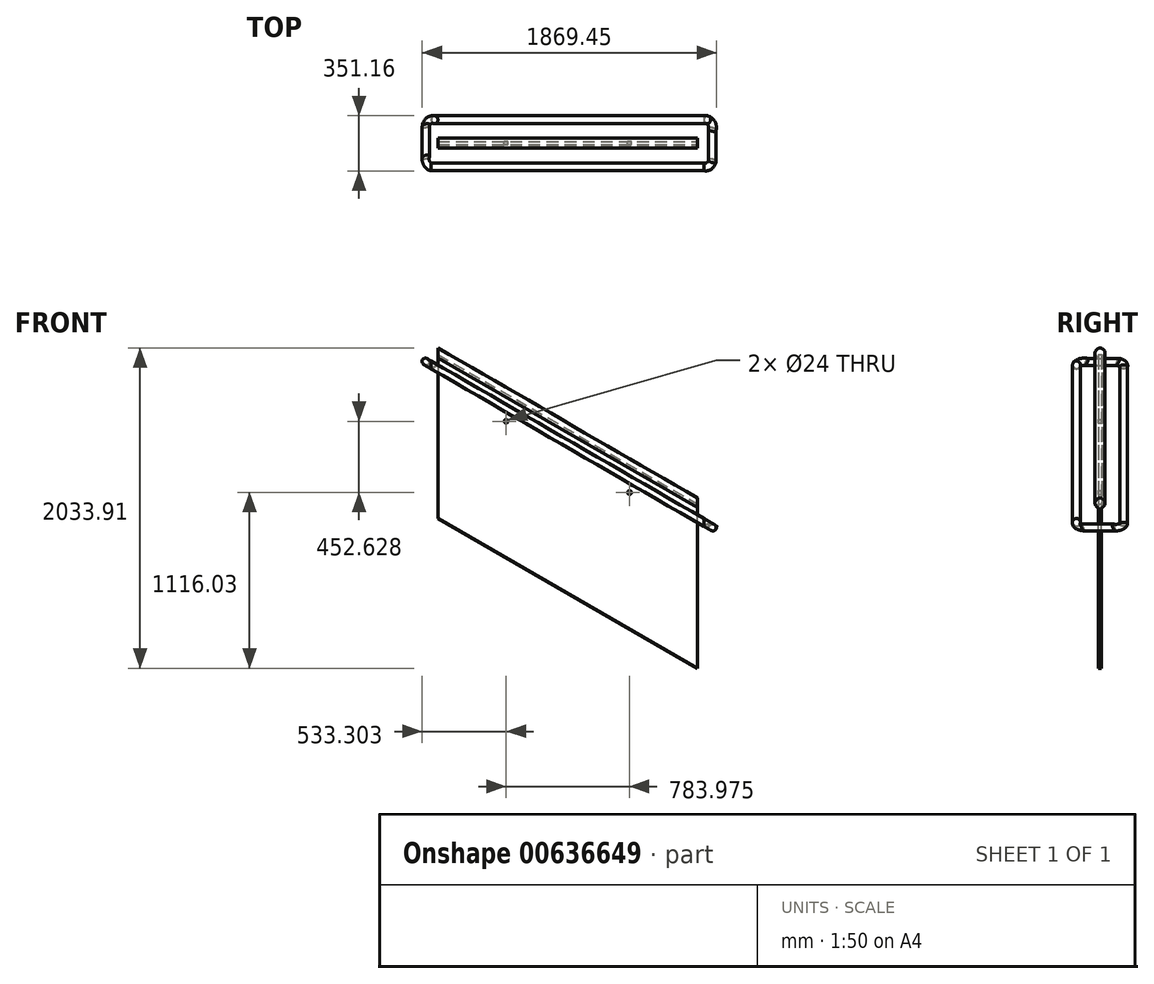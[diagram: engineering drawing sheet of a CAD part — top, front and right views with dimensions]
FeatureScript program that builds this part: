
annotation { "Feature Type Name" : "Feature", "Feature Type Description" : "" }
export const myFeature = defineFeature(function(context is Context, id is Id, definition is map)
    precondition{}
    {
        {
            var Q0;
            Q0=qCreatedBy(makeId("Front.planeOp"),FACE);
            var sketch = newSketch(context, id + "F0", { "sketchPlane" : qUnion([Q0])});
            skLineSegment(sketch, "E0", {"start": v(0, 0) * mm, "end": v(1650, -952.63) * mm});
            skLineSegment(sketch, "E1", {"start": v(1650, -952.63) * mm, "end": v(1650, 86.6) * mm});
            skLineSegment(sketch, "E2", {"start": v(1650, 86.6) * mm, "end": v(0, 1039.23) * mm});
            skLineSegment(sketch, "E3.0", {"start": v(1650, -86.6) * mm, "end": v(0, 866.03) * mm, "construction": true});
            skCircle(sketch, "E4", {"center": v(433.01, 616.03) * mm, "radius": 12 * mm});
            skCircle(sketch, "E5", {"center": v(1216.99, 163.4) * mm, "radius": 12 * mm});
            skLineSegment(sketch, "E6", {"start": v(0, 1039.23) * mm, "end": v(0, 0) * mm});
            skSolve(sketch);
        }
        {
            var Q0;
            Q0=qSketchRegion(id+"F0",true);
            extrude(context, id + "F1", {"entities" : qUnion([Q0]), "endBound" : BoundingType.SYMMETRIC, "depth" : 19 * mm, "offsetDistance" : 25 * mm});
        }
        {
            var Q0;
            Q0=qCreatedBy(makeId("Front.planeOp"),FACE);
            var sketch = newSketch(context, id + "F2", { "sketchPlane" : qUnion([Q0])});
            skLineSegment(sketch, "E7.1", {"start": v(1650, 86.6) * mm, "end": v(0, 1039.23) * mm});
            skSolve(sketch);
        }
        {
            var Q0;
            Q0=qCreatedBy(makeId("Right.planeOp"),FACE);
            var sketch = newSketch(context, id + "F3", { "sketchPlane" : qUnion([Q0])});
            skLineSegment(sketch, "E8", {"start": v(9.5, 1019.23) * mm, "end": v(9.5, 1039.23) * mm});
            skLineSegment(sketch, "E9.0", {"start": v(-9.5, 1039.23) * mm, "end": v(9.5, 1039.23) * mm});
            skLineSegment(sketch, "E10", {"start": v(-9.5, 1039.23) * mm, "end": v(-9.5, 1019.23) * mm});
            skArc(sketch, "E11", {"start": v(9.5, 1019.23) * mm, "mid": v(0, 1081.28) * mm, "end": v(-9.5, 1019.23) * mm});
            skArc(sketch, "E12.0", {"start": v(11, 1021.35) * mm, "mid": v(0, 1079.78) * mm, "end": v(-11, 1021.35) * mm});
            skLineSegment(sketch, "E12.1", {"start": v(11, 1021.35) * mm, "end": v(11, 1040.73) * mm});
            skLineSegment(sketch, "E12.2", {"start": v(-11, 1040.73) * mm, "end": v(11, 1040.73) * mm});
            skLineSegment(sketch, "E12.3", {"start": v(-11, 1040.73) * mm, "end": v(-11, 1021.35) * mm});
            skSolve(sketch);
        }
        {
            var Q0;
            Q0=qSketchRegion(id+"F3",true);
            var Q1;
            Q1=sQuery(id+"F2.wireOp",EDGE,"E7.0");
            var Q2;
            Q2=sQuery(id+"F2.wireOp",EDGE,"E7.1");
            sweep(context, id + "F4", {"profiles" : qUnion([Q0]), "path" : qUnion([Q1, Q2])});
        }
        {
            var Q0;
            Q0=makeQuery(id+"F4.opSweep","CAP_FACE",FACE,{"disambiguationData":[OSD([sQuery(id+"F2.wireOp",VERTEX,"E7.1.start"),sQuery(id+"F3.wireOp",EDGE,"E8"),sQuery(id+"F3.wireOp",EDGE,"E9.0"),sQuery(id+"F3.wireOp",EDGE,"E10"),sQuery(id+"F3.wireOp",EDGE,"E11"),sQuery(id+"F3.wireOp",EDGE,"E12.0"),sQuery(id+"F3.wireOp",EDGE,"E12.1"),sQuery(id+"F3.wireOp",EDGE,"E12.2"),sQuery(id+"F3.wireOp",EDGE,"E12.3")])],"isStart":false});
            var sketch = newSketch(context, id + "F5", { "sketchPlane" : qUnion([Q0])});
            skCircle(sketch, "E13", {"center": v(0, 96.9) * mm, "radius": 31.75 * mm});
            skSolve(sketch);
        }
        {
            var Q0;
            Q0=qSketchRegion(id+"F5",true);
            extrude(context, id + "F6", {"entities" : qUnion([Q0]), "operationType" : NewBodyOperationType.ADD, "oppositeDirection" : true, "depth" : 2 * mm, "offsetDistance" : 25 * mm});
        }
        {
            var Q0;
            Q0=qCreatedBy(makeId("Top.planeOp"),FACE);
            var Q1;
            Q1=sQuery(id+"F0.wireOp",EDGE,"E3.0");
            cPlane(context, id + "F7", {"entities" : qUnion([Q0, Q1]), "cplaneType" : CPlaneType.LINE_ANGLE, "offset" : 100 * mm, "angle" : 0 * degree, "width" : 150 * mm, "height" : 150 * mm});
        }
        {
            var Q0;
            Q0=qCreatedBy(id+"F7.planeOp",FACE);
            cPlane(context, id + "F8", {"entities" : qUnion([Q0]), "cplaneType" : CPlaneType.OFFSET, "offset" : 50 * mm, "oppositeDirection" : true, "width" : 150 * mm, "height" : 150 * mm});
        }
        {
            var Q0;
            Q0=qCreatedBy(id+"F8.planeOp",FACE);
            var sketch = newSketch(context, id + "F9", { "sketchPlane" : qUnion([Q0])});
            skLineSegment(sketch, "E14.1", {"start": v(-511.88, -149.45) * mm, "end": v(1488.12, -149.45) * mm});
            skLineSegment(sketch, "E15", {"start": v(-511.88, 149.45) * mm, "end": v(1488.12, 149.45) * mm});
            skLineSegment(sketch, "E16", {"start": v(-561.88, -99.45) * mm, "end": v(-561.88, 99.45) * mm});
            skLineSegment(sketch, "E17", {"start": v(1538.12, -99.45) * mm, "end": v(1538.12, 99.45) * mm});
            skPoint(sketch, "E18.visualSharp", {"position": v(-561.88, -149.45) * mm});
            skArc(sketch, "E18.filletArc", {"start": v(-561.88, -99.45) * mm, "mid": v(-547.24, -134.8) * mm, "end": v(-511.88, -149.45) * mm});
            skPoint(sketch, "E19.visualSharp", {"position": v(-561.88, 149.45) * mm});
            skArc(sketch, "E19.filletArc", {"start": v(-511.88, 149.45) * mm, "mid": v(-547.24, 134.8) * mm, "end": v(-561.88, 99.45) * mm});
            skPoint(sketch, "E20.visualSharp", {"position": v(1538.12, 149.45) * mm});
            skArc(sketch, "E20.filletArc", {"start": v(1538.12, 99.45) * mm, "mid": v(1523.48, 134.8) * mm, "end": v(1488.12, 149.45) * mm});
            skPoint(sketch, "E21.visualSharp", {"position": v(1538.12, -149.45) * mm});
            skArc(sketch, "E21.filletArc", {"start": v(1488.12, -149.45) * mm, "mid": v(1523.48, -134.8) * mm, "end": v(1538.12, -99.45) * mm});
            skSolve(sketch);
        }
        {
            var Q0;
            Q0=qCreatedBy(makeId("Right.planeOp"),FACE);
            var sketch = newSketch(context, id + "F10", { "sketchPlane" : qUnion([Q0])});
            skCircle(sketch, "E22", {"center": v(-149.45, 948.76) * mm, "radius": 25 * mm});
            skCircle(sketch, "E23.0", {"center": v(-149.45, 948.76) * mm, "radius": 23 * mm});
            skSolve(sketch);
        }
        {
            var Q0;
            Q0=makeQuery(id+"F10.imprint","IMPRINT",FACE,{"disambiguationData":[TD([[makeQuery(id+"F10.imprint","IMPRINT",EDGE,{"derivedFrom":sQuery(id+"F10.wireOp",EDGE,"E22")}),1.0]])]});
            var Q1;
            Q1=sQuery(id+"F9.wireOp",EDGE,"E15");
            var Q2;
            Q2=sQuery(id+"F9.wireOp",EDGE,"E19.filletArc");
            var Q3;
            Q3=sQuery(id+"F9.wireOp",EDGE,"E16");
            var Q4;
            Q4=sQuery(id+"F9.wireOp",EDGE,"E18.filletArc");
            var Q5;
            Q5=sQuery(id+"F9.wireOp",EDGE,"E14.1");
            var Q6;
            Q6=sQuery(id+"F9.wireOp",EDGE,"E21.filletArc");
            var Q7;
            Q7=sQuery(id+"F9.wireOp",EDGE,"E17");
            var Q8;
            Q8=sQuery(id+"F9.wireOp",EDGE,"E20.filletArc");
            sweep(context, id + "F11", {"profiles" : qUnion([Q0]), "path" : qUnion([Q1, Q2, Q3, Q4, Q5, Q6, Q7, Q8])});
        }
    });
